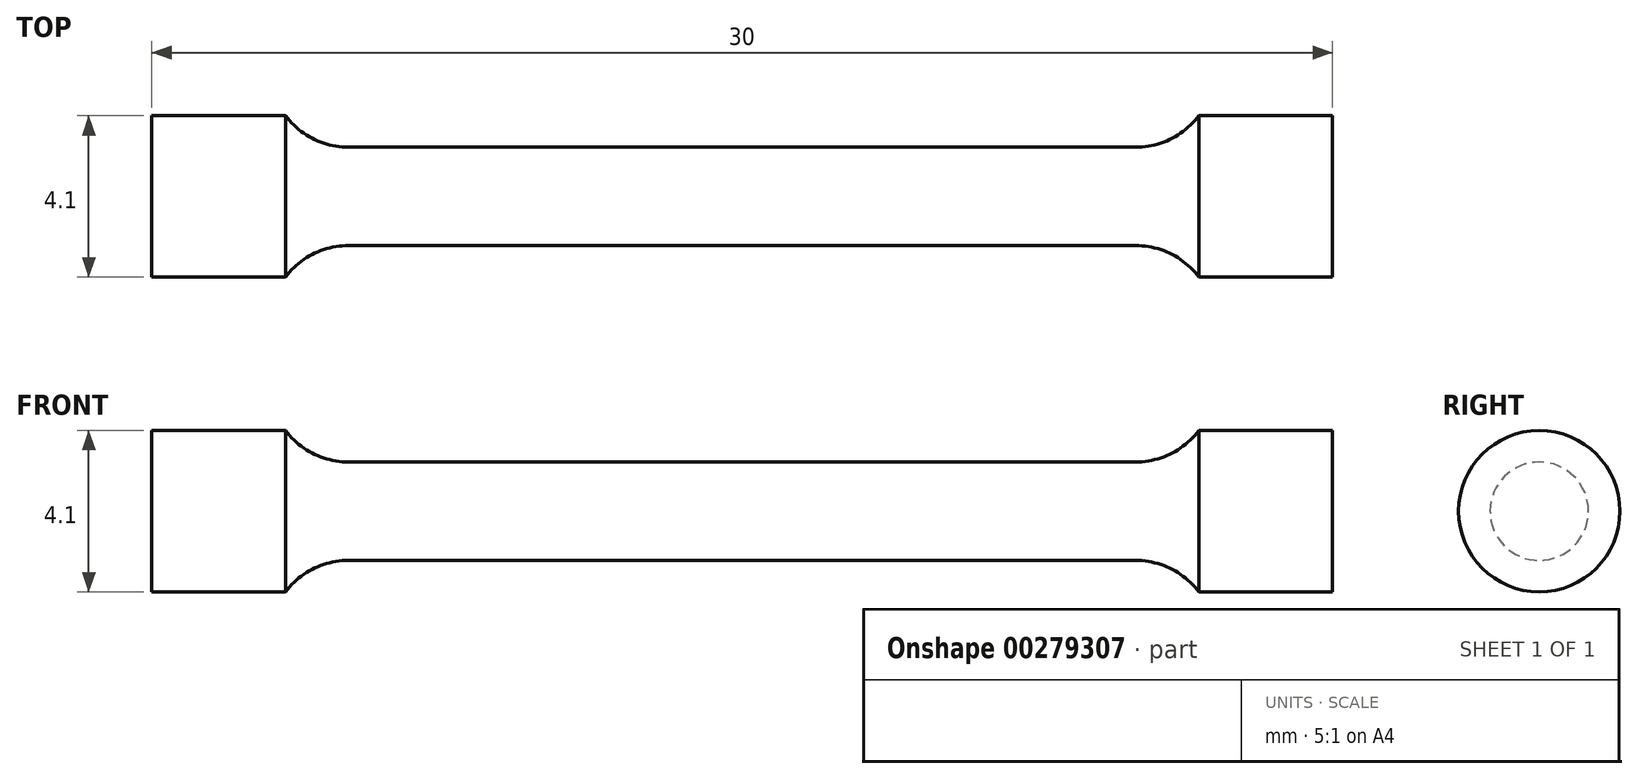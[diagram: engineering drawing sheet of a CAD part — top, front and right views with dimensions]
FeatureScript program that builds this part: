
annotation { "Feature Type Name" : "Feature", "Feature Type Description" : "" }
export const myFeature = defineFeature(function(context is Context, id is Id, definition is map)
    precondition{}
    {
        {
            var Q0;
            Q0=qCreatedBy(makeId("Front.planeOp"),FACE);
            var sketch = newSketch(context, id + "F0", { "sketchPlane" : qUnion([Q0])});
            skLineSegment(sketch, "E0", {"start": v(0, 1.25) * mm, "end": v(10, 1.25) * mm});
            skArc(sketch, "E1", {"start": v(10, 1.25) * mm, "mid": v(10.9, 1.46) * mm, "end": v(11.6, 2.05) * mm});
            skLineSegment(sketch, "E2", {"start": v(11.6, 2.05) * mm, "end": v(15, 2.05) * mm});
            skLineSegment(sketch, "E3", {"start": v(15, 2.05) * mm, "end": v(15, 0) * mm});
            skLineSegment(sketch, "E4.MirrorCS", {"start": v(0, 1.25) * mm, "end": v(-10, 1.25) * mm});
            skLineSegment(sketch, "E5.MirrorCS", {"start": v(-15, 2.05) * mm, "end": v(-15, 0) * mm});
            skLineSegment(sketch, "E6.MirrorCS", {"start": v(-11.6, 2.05) * mm, "end": v(-15, 2.05) * mm});
            skArc(sketch, "E7.MirrorCS", {"start": v(-10, 1.25) * mm, "mid": v(-10.9, 1.46) * mm, "end": v(-11.6, 2.05) * mm});
            skLineSegment(sketch, "E8", {"start": v(-15, 0) * mm, "end": v(15, 0) * mm});
            skSolve(sketch);
        }
        {
            var Q0;
            Q0=makeQuery(id+"F0.imprint","IMPRINT",FACE,{"disambiguationData":[TD([[makeQuery(id+"F0.imprint","IMPRINT",EDGE,{"derivedFrom":sQuery(id+"F0.wireOp",EDGE,"E0")}),-1.0]])]});
            var Q1;
            Q1=sQuery(id+"F0.wireOp",EDGE,"E8");
            revolve(context, id + "F1", {"entities" : qUnion([Q0]), "axis" : qUnion([Q1]), "revolveType" : RevolveType.FULL});
        }
    });
